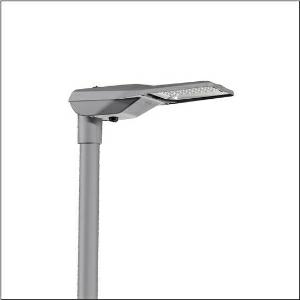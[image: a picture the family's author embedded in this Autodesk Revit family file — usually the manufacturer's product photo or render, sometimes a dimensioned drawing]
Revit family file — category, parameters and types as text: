
# Revit family: streetlight_sl_21_iq_mini___st1_0a_5xe2d61y08hb_d678
name_source: partatom
category: Lighting Fixtures
units: mm (PartAtom-declared; Revit-internal decimal feet)

## family parameters
Cut with Voids When Loaded = No
Host = Face
Light Source = No
Part Type = Normal
Room Calculation Point = No
Round Connector Dimension = Use Diameter
Shared = No

## types (1)
- --- (1 x LED, 8460 lm, 71 W, 2700K)
    Apparent Load = 71 VA
    CIE Flux Codes = 37 72 97 100 100
    Color Rendering = 70
    Color Temperature = 2700K
    Default Elevation = 1800 mm
    Description = Streetlight SL 21 iQ mini, mast luminaire, primary light control with lens, of PMMA, primary optical cover: cover, of toughened safety glass, transparent, light distribution: ST1.0a, light emission: direct distribution, primary light characteristic: asymmetric, installation type: post-top, side-entry, LED, High Power LED, rated luminous flux: 8.460lm, luminous efficacy: 119lm/W, light colour: 727, colour temperature: 2700K, control gear: iQ-Street Remote, D4i with power reduction, control: pre-setting: logarithmic dimming characteristic, Street-Remote, Auto-Match, Temp-Guard, Lumen-Switch, Night-Set, Smart-Wire, Light-Fading, Desk-Remote (wireless, voltage-free reading and setting of iQ features in the workshop via application-optimized NFC function/RFID function), optimised constant luminous flux control (CLO 2.0), mains connection: 220..240V, AC, 50/60Hz, start of lifetime: 71W, end of service life: 75W, reduction: 30W, luminaire housing, of diecast aluminium, powder-coated, Siteco® metallic grey (DB 702S), corrosivity category C5 mid according to DIN EN ISO 12944, please order mast flange separately, inclination adjustable: 0°, 5°, 10°, 15°, sealing non-destructively replaceable, multi-level sealing system, length: 628mm, width: 235mm, height: 110mm, mast flange for spigot size: 42mm (side-entry): 5XC10008XM4, 60/48mm (side-entry/post-top): 5XC10108XM2, 76/60mm (side-entry/post-top): 5XC10108XM1, mounting height: 4..8m, Smart Interface below and above, protection rating (complete): IP66, insulation class (complete): insulation class II (safety insulation), certification: CE, ENEC, ENEC+, VDE, impact resistance: IK10, permissible operating ambient temperature for outdoor applications: -40..+50°C, standard-compliant lighting for roads and squares, packaging unit: 1 piece

Light Distribution: ST1.0a
    Height = 110 mm
    Lamp = 1 x LED
    Lamp Light Flux = 8460 lm
    Lamp Power = 71 W
    Lamp count = 1
    Length = 625 mm
    Luminous efficacy = 119 lm/W
    Manufacturer = Siteco
    ModVariant = No
    Model = 5XE2D61Y08HB
    Number of Poles = 1
    OnlyDefault = Yes
    Power Factor = 1
    Product Name = Streetlight SL 21 iQ mini | ST1.0a
    Product group = mast luminaire | pylon top
    ProductGroupID = 6100
    Protection Class = Protection class II
    Protection Degree = IP 66
    RLX_Detail_Level = 1
    RLX_Emergency_Light_Flux = 0 lm
    RLX_Emergency_Type = 0
    RLX_Emergency_Type_DB = No
    RlxData = <blob elided: 26645 chars, md5=41c06e43>
    Socket = socket
    Standby Power = 0 W
    System Light Flux = 8460 lm
    System Power = 71 W
    Type Comments = factory setting: luminous flux: 100 % | dim-lin: 254 | 716 mA
    Type Image = l_1003514.jpg
    URL = http://relux.com
    VarID = @adj_114954
    Voltage = 0 V
    Weight = 0.00 kg
    Width = 234 mm

## geometry (parser evidence)
native form markers: Blend x4, Sweep x11
no freeform markers — native parametric forms only
